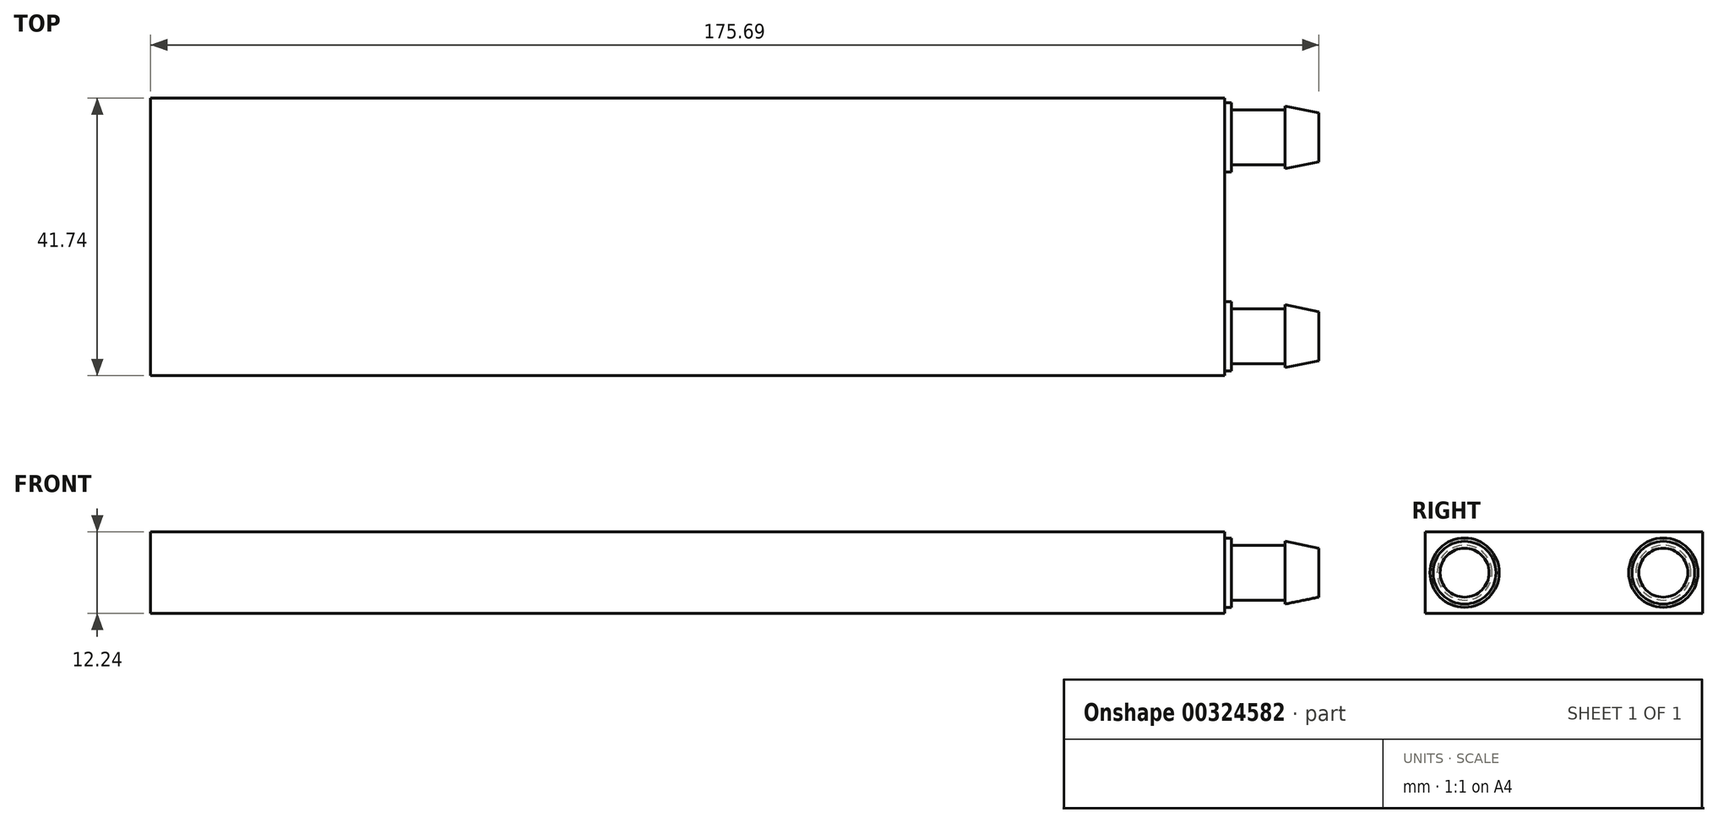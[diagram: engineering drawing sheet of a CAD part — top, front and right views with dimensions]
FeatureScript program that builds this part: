
annotation { "Feature Type Name" : "Feature", "Feature Type Description" : "" }
export const myFeature = defineFeature(function(context is Context, id is Id, definition is map)
    precondition{}
    {
        {
            var Q0;
            Q0=qCreatedBy(makeId("Top.planeOp"),FACE);
            var sketch = newSketch(context, id + "F0", { "sketchPlane" : qUnion([Q0])});
            skLineSegment(sketch, "E0.bottom", {"start": v(-80.76, 20.87) * mm, "end": v(80.76, 20.87) * mm});
            skLineSegment(sketch, "E0.top", {"start": v(-80.76, -20.87) * mm, "end": v(80.76, -20.87) * mm});
            skLineSegment(sketch, "E0.left", {"start": v(-80.76, 20.87) * mm, "end": v(-80.76, -20.87) * mm});
            skLineSegment(sketch, "E0.right", {"start": v(80.76, 20.87) * mm, "end": v(80.76, -20.87) * mm});
            skPoint(sketch, "E1", {"position": v(80.76, 0) * mm});
            skPoint(sketch, "E2", {"position": v(0, 20.87) * mm});
            skSolve(sketch);
        }
        {
            var Q0;
            Q0=makeQuery(id+"F0.imprint","IMPRINT",FACE,{"disambiguationData":[TD([[makeQuery(id+"F0.imprint","IMPRINT",EDGE,{"derivedFrom":sQuery(id+"F0.wireOp",EDGE,"E0.bottom")}),-1.0]])]});
            extrude(context, id + "F1", {"entities" : qUnion([Q0]), "endBound" : BoundingType.SYMMETRIC, "depth" : 12.24 * mm});
        }
        {
            var Q0;
            Q0=qCreatedBy(makeId("Top.planeOp"),FACE);
            var sketch = newSketch(context, id + "F2", { "sketchPlane" : qUnion([Q0])});
            skLineSegment(sketch, "E3", {"start": v(-80.76, 0) * mm, "end": v(80.76, 0) * mm, "construction": true});
            skLineSegment(sketch, "E4", {"start": v(80.76, -19.08) * mm, "end": v(89.85, -19.08) * mm});
            skLineSegment(sketch, "E5", {"start": v(89.85, -19.08) * mm, "end": v(89.85, -19.67) * mm});
            skLineSegment(sketch, "E6", {"start": v(89.85, -19.67) * mm, "end": v(94.93, -18.63) * mm});
            skLineSegment(sketch, "E7", {"start": v(94.93, -18.63) * mm, "end": v(94.93, -14.95) * mm});
            skLineSegment(sketch, "E8", {"start": v(94.93, -14.95) * mm, "end": v(80.76, -14.95) * mm});
            skLineSegment(sketch, "E9", {"start": v(80.76, -14.95) * mm, "end": v(80.76, -19.08) * mm});
            skLineSegment(sketch, "E10", {"start": v(80.76, -19.08) * mm, "end": v(80.76, -10.82) * mm, "construction": true});
            skLineSegment(sketch, "E11", {"start": v(80.76, 19.08) * mm, "end": v(80.76, 10.82) * mm, "construction": true});
            skLineSegment(sketch, "E12", {"start": v(89.85, -19.67) * mm, "end": v(89.85, -10.22) * mm, "construction": true});
            skLineSegment(sketch, "E13", {"start": v(94.93, -18.63) * mm, "end": v(94.93, -11.26) * mm, "construction": true});
            skSolve(sketch);
        }
        {
            var Q0;
            Q0 = qSketchRegion(id + "F2", true);
            var Q1;
            Q1=sQuery(id+"F2.wireOp",EDGE,"E8");
            revolve(context, id + "F3", {"operationType" : NewBodyOperationType.ADD, "entities" : qUnion([Q0]), "axis" : qUnion([Q1]), "revolveType" : RevolveType.FULL});
        }
        {
            var Q0;
            Q0=makeQuery(id+"F1.opExtrude","SWEPT_BODY",BODY,{"disambiguationData":[OSD([sQuery(id+"F0.wireOp",EDGE,"E0.bottom"),sQuery(id+"F0.wireOp",EDGE,"E0.top"),sQuery(id+"F0.wireOp",EDGE,"E0.left"),sQuery(id+"F0.wireOp",EDGE,"E0.right")])]});
            var Q1;
            Q1=qCreatedBy(makeId("Front.planeOp"),FACE);
            mirror(context, id + "F4", {"operationType" : NewBodyOperationType.ADD, "entities" : qUnion([Q0]), "mirrorPlane" : qUnion([Q1])});
        }
        {
            var Q0;
            Q0=makeQuery(id+"F1.opExtrude","CAP_FACE",FACE,{"disambiguationData":[OSD([sQuery(id+"F0.wireOp",EDGE,"E0.bottom"),sQuery(id+"F0.wireOp",EDGE,"E0.top"),sQuery(id+"F0.wireOp",EDGE,"E0.left"),sQuery(id+"F0.wireOp",EDGE,"E0.right")])],"isStart":false});
            var sketch = newSketch(context, id + "F5", { "sketchPlane" : qUnion([Q0])});
            skLineSegment(sketch, "E14", {"start": v(-80.76, 0) * mm, "end": v(-40.38, 0) * mm, "construction": true});
            skLineSegment(sketch, "E15", {"start": v(-40.38, 0) * mm, "end": v(0, 0) * mm, "construction": true});
            skLineSegment(sketch, "E16", {"start": v(0, 0) * mm, "end": v(40.38, 0) * mm, "construction": true});
            skLineSegment(sketch, "E17", {"start": v(40.38, 0) * mm, "end": v(80.76, 0) * mm, "construction": true});
            skPoint(sketch, "E18", {"position": v(-60.57, 0) * mm});
            skPoint(sketch, "E19", {"position": v(-20.19, 0) * mm});
            skPoint(sketch, "E20", {"position": v(20.19, 0) * mm});
            skPoint(sketch, "E21", {"position": v(60.57, 0) * mm});
            skSolve(sketch);
        }
        {
            var Q0;
            Q0=makeQuery(id+"F1.opExtrude","CAP_FACE",FACE,{"disambiguationData":[OSD([sQuery(id+"F0.wireOp",EDGE,"E0.bottom"),sQuery(id+"F0.wireOp",EDGE,"E0.top"),sQuery(id+"F0.wireOp",EDGE,"E0.left"),sQuery(id+"F0.wireOp",EDGE,"E0.right")])],"isStart":true});
            var sketch = newSketch(context, id + "F6", { "sketchPlane" : qUnion([Q0])});
            skLineSegment(sketch, "E22", {"start": v(-80.76, 0) * mm, "end": v(-40.38, 0) * mm, "construction": true});
            skLineSegment(sketch, "E23", {"start": v(-40.38, 0) * mm, "end": v(0, 0) * mm, "construction": true});
            skLineSegment(sketch, "E24", {"start": v(0, 0) * mm, "end": v(40.38, 0) * mm, "construction": true});
            skLineSegment(sketch, "E25", {"start": v(40.38, 0) * mm, "end": v(80.76, 0) * mm, "construction": true});
            skPoint(sketch, "E26", {"position": v(-60.57, 0) * mm});
            skPoint(sketch, "E27", {"position": v(-20.19, 0) * mm});
            skPoint(sketch, "E28", {"position": v(20.19, 0) * mm});
            skPoint(sketch, "E29", {"position": v(60.57, 0) * mm});
            skSolve(sketch);
        }
        {
            var Q0;
            Q0=makeQuery(id+"F1.opExtrude","SWEPT_FACE",FACE,{"disambiguationData":[OSD([sQuery(id+"F0.wireOp",EDGE,"E0.right")])]});
            var sketch = newSketch(context, id + "F7", { "sketchPlane" : qUnion([Q0])});
            skCircle(sketch, "E30", {"center": v(-14.95, 0) * mm, "radius": 5.2 * mm});
            skCircle(sketch, "E31", {"center": v(14.95, 0) * mm, "radius": 5.2 * mm});
            skSolve(sketch);
        }
        {
            var Q0;
            Q0=makeQuery(id+"F7.imprint","IMPRINT",FACE,{"disambiguationData":[TD([[makeQuery(id+"F7.imprint","IMPRINT",EDGE,{"derivedFrom":sQuery(id+"F7.wireOp",EDGE,"E30")}),1.0]])]});
            var Q1;
            Q1=makeQuery(id+"F7.imprint","IMPRINT",FACE,{"disambiguationData":[TD([[makeQuery(id+"F7.imprint","IMPRINT",EDGE,{"derivedFrom":sQuery(id+"F7.wireOp",EDGE,"E31")}),1.0]])]});
            extrude(context, id + "F8", {"entities" : qUnion([Q0, Q1]), "operationType" : NewBodyOperationType.ADD, "depth" : 1.02 * mm});
        }
    });
